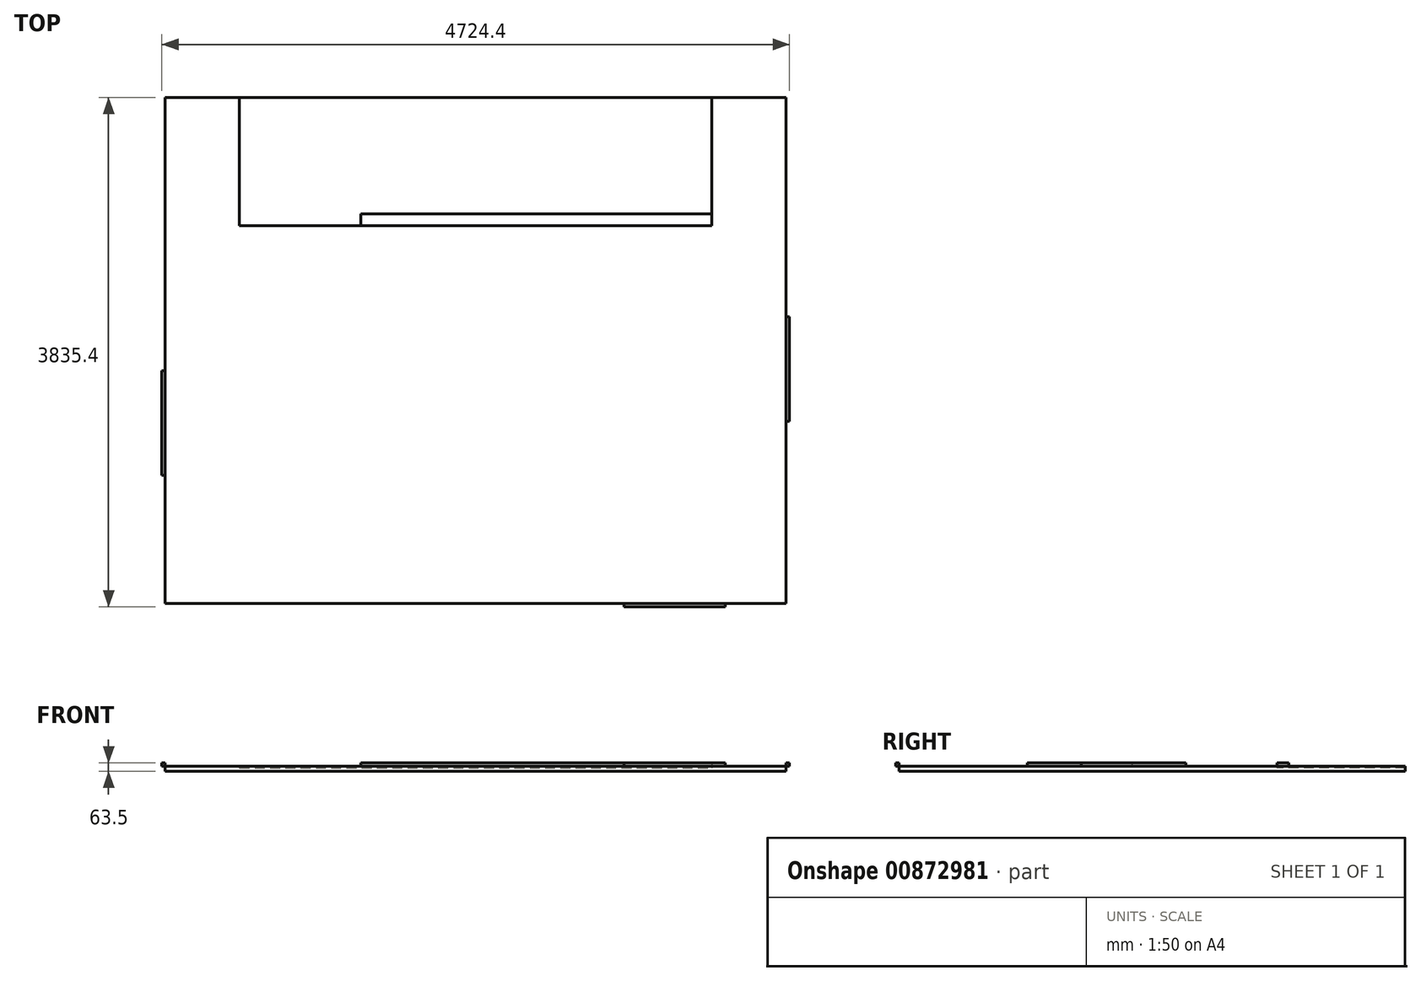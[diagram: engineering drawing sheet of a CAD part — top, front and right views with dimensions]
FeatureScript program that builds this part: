
annotation { "Feature Type Name" : "Feature", "Feature Type Description" : "" }
export const myFeature = defineFeature(function(context is Context, id is Id, definition is map)
    precondition{}
    {
        {
            var Q0;
            Q0=qCreatedBy(makeId("Top.planeOp"),FACE);
            var sketch = newSketch(context, id + "F0", { "sketchPlane" : qUnion([Q0])});
            skLineSegment(sketch, "E0", {"start": v(0, 0) * mm, "end": v(0, 3810) * mm});
            skLineSegment(sketch, "E1", {"start": v(0, 3810) * mm, "end": v(4673.6, 3810) * mm});
            skLineSegment(sketch, "E2", {"start": v(4673.6, 3810) * mm, "end": v(4673.6, 0) * mm});
            skLineSegment(sketch, "E3", {"start": v(4673.6, 0) * mm, "end": v(0, 0) * mm});
            skSolve(sketch);
        }
        {
            var Q0;
            Q0 = qSketchRegion(id + "F0", true);
            extrude(context, id + "F1", {"entities" : qUnion([Q0]), "depth" : 25.4 * mm, "offsetDistance" : 25.4 * mm});
        }
        {
            var Q0;
            Q0=makeQuery(id+"F1.opExtrude","CAP_FACE",FACE,{"disambiguationData":[OSD([sQuery(id+"F0.wireOp",EDGE,"E0"),sQuery(id+"F0.wireOp",EDGE,"E1"),sQuery(id+"F0.wireOp",EDGE,"E2"),sQuery(id+"F0.wireOp",EDGE,"E3")])],"isStart":false});
            var sketch = newSketch(context, id + "F2", { "sketchPlane" : qUnion([Q0])});
            skLineSegment(sketch, "E4", {"start": v(558.8, 3810) * mm, "end": v(558.8, 2844.8) * mm});
            skLineSegment(sketch, "E5", {"start": v(558.8, 2844.8) * mm, "end": v(4114.8, 2844.8) * mm});
            skLineSegment(sketch, "E6", {"start": v(4114.8, 2844.8) * mm, "end": v(4114.8, 3810) * mm});
            skLineSegment(sketch, "E7.0.0", {"start": v(0, 0) * mm, "end": v(4673.6, 0) * mm});
            skLineSegment(sketch, "E7.0.1", {"start": v(4673.6, 0) * mm, "end": v(4673.6, 3810) * mm});
            skLineSegment(sketch, "E7.0.2", {"start": v(4673.6, 3810) * mm, "end": v(0, 3810) * mm});
            skLineSegment(sketch, "E7.0.3", {"start": v(0, 3810) * mm, "end": v(0, 0) * mm});
            skSolve(sketch);
        }
        {
            var Q0;
            {var subQ1=sQuery(id+"F2.wireOp",EDGE,"E4");Q0=makeQuery(id+"F2.imprint","IMPRINT",FACE,{"disambiguationData":[TD([[makeQuery(id+"F2.imprint","IMPRINT",EDGE,{"derivedFrom":subQ1}),-1.0]])]});}
            extrude(context, id + "F3", {"entities" : qUnion([Q0]), "operationType" : NewBodyOperationType.ADD, "depth" : 12.7 * mm, "offsetDistance" : 25.4 * mm});
        }
        {
            var Q0;
            Q0=makeQuery(id+"F3.opExtrude","CAP_FACE",FACE,{"disambiguationData":[OSD([sQuery(id+"F2.wireOp",EDGE,"E4"),sQuery(id+"F2.wireOp",EDGE,"E5"),sQuery(id+"F2.wireOp",EDGE,"E6"),sQuery(id+"F2.wireOp",EDGE,"E7.0.0"),sQuery(id+"F2.wireOp",EDGE,"E7.0.1"),sQuery(id+"F2.wireOp",EDGE,"E7.0.2"),sQuery(id+"F2.wireOp",EDGE,"E7.0.3")])],"isStart":false});
            var sketch = newSketch(context, id + "F4", { "sketchPlane" : qUnion([Q0])});
            skLineSegment(sketch, "E8", {"start": v(4114.8, 2844.8) * mm, "end": v(1473.2, 2844.8) * mm});
            skLineSegment(sketch, "E9", {"start": v(1473.2, 2844.8) * mm, "end": v(1473.2, 2933.7) * mm});
            skLineSegment(sketch, "E10", {"start": v(1473.2, 2933.7) * mm, "end": v(4114.8, 2933.7) * mm});
            skLineSegment(sketch, "E11", {"start": v(4114.8, 2933.7) * mm, "end": v(4114.8, 2844.8) * mm});
            skLineSegment(sketch, "E12.0", {"start": v(4114.8, 2844.8) * mm, "end": v(4114.8, 3810) * mm});
            skLineSegment(sketch, "E13.0.0", {"start": v(558.8, 2844.8) * mm, "end": v(4114.8, 2844.8) * mm});
            skLineSegment(sketch, "E13.0.2", {"start": v(4114.8, 3810) * mm, "end": v(558.8, 3810) * mm});
            skLineSegment(sketch, "E13.0.3", {"start": v(558.8, 3810) * mm, "end": v(558.8, 2844.8) * mm});
            skLineSegment(sketch, "E14.0", {"start": v(4673.6, 3810) * mm, "end": v(4673.6, 0) * mm});
            skSolve(sketch);
        }
        {
            var Q0;
            {var subQ0=sQuery(id+"F4.wireOp",EDGE,"E9");Q0=makeQuery(id+"F4.imprint","IMPRINT",FACE,{"disambiguationData":[TD([[makeQuery(id+"F4.imprint","IMPRINT",EDGE,{"derivedFrom":subQ0}),-1.0]])]});}
            extrude(context, id + "F5", {"entities" : qUnion([Q0]), "depth" : 25.4 * mm, "offsetDistance" : 25.4 * mm});
        }
        {
            var Q0;
            Q0=makeQuery(id+"F3.opExtrude","CAP_FACE",FACE,{"disambiguationData":[OSD([sQuery(id+"F2.wireOp",EDGE,"E4"),sQuery(id+"F2.wireOp",EDGE,"E5"),sQuery(id+"F2.wireOp",EDGE,"E6"),sQuery(id+"F2.wireOp",EDGE,"E7.0.0"),sQuery(id+"F2.wireOp",EDGE,"E7.0.1"),sQuery(id+"F2.wireOp",EDGE,"E7.0.2"),sQuery(id+"F2.wireOp",EDGE,"E7.0.3")])],"isStart":false});
            var sketch = newSketch(context, id + "F6", { "sketchPlane" : qUnion([Q0])});
            skLineSegment(sketch, "E15.bottom", {"start": v(0, 965.2) * mm, "end": v(-25.4, 965.2) * mm});
            skLineSegment(sketch, "E15.top", {"start": v(0, 1752.6) * mm, "end": v(-25.4, 1752.6) * mm});
            skLineSegment(sketch, "E15.left", {"start": v(0, 965.2) * mm, "end": v(0, 1752.6) * mm});
            skLineSegment(sketch, "E15.right", {"start": v(-25.4, 965.2) * mm, "end": v(-25.4, 1752.6) * mm});
            skLineSegment(sketch, "E16.0.0", {"start": v(4114.8, 3810) * mm, "end": v(4114.8, 2844.8) * mm});
            skLineSegment(sketch, "E16.0.1", {"start": v(4114.8, 2844.8) * mm, "end": v(558.8, 2844.8) * mm});
            skLineSegment(sketch, "E16.0.2", {"start": v(558.8, 2844.8) * mm, "end": v(558.8, 3810) * mm});
            skLineSegment(sketch, "E16.0.3", {"start": v(558.8, 3810) * mm, "end": v(0, 3810) * mm});
            skLineSegment(sketch, "E16.0.4", {"start": v(0, 3810) * mm, "end": v(0, 0) * mm});
            skLineSegment(sketch, "E16.0.5", {"start": v(0, 0) * mm, "end": v(4673.6, 0) * mm});
            skLineSegment(sketch, "E16.0.6", {"start": v(4673.6, 0) * mm, "end": v(4673.6, 3810) * mm});
            skLineSegment(sketch, "E16.0.7", {"start": v(4673.6, 3810) * mm, "end": v(4114.8, 3810) * mm});
            skSolve(sketch);
        }
        {
            var Q0;
            {var subQ0=sQuery(id+"F6.wireOp",EDGE,"E15.bottom");Q0=makeQuery(id+"F6.imprint","IMPRINT",FACE,{"disambiguationData":[TD([[makeQuery(id+"F6.imprint","IMPRINT",EDGE,{"derivedFrom":subQ0}),-1.0]])]});}
            extrude(context, id + "F7", {"entities" : qUnion([Q0]), "depth" : 25.4 * mm, "offsetDistance" : 25.4 * mm});
        }
        {
            var Q0;
            Q0=makeQuery(id+"F3.opExtrude","CAP_FACE",FACE,{"disambiguationData":[OSD([sQuery(id+"F2.wireOp",EDGE,"E4"),sQuery(id+"F2.wireOp",EDGE,"E5"),sQuery(id+"F2.wireOp",EDGE,"E6"),sQuery(id+"F2.wireOp",EDGE,"E7.0.0"),sQuery(id+"F2.wireOp",EDGE,"E7.0.1"),sQuery(id+"F2.wireOp",EDGE,"E7.0.2"),sQuery(id+"F2.wireOp",EDGE,"E7.0.3")])],"isStart":false});
            var sketch = newSketch(context, id + "F8", { "sketchPlane" : qUnion([Q0])});
            skLineSegment(sketch, "E17.0", {"start": v(4673.6, 3810) * mm, "end": v(4673.6, 0) * mm});
            skLineSegment(sketch, "E18.bottom", {"start": v(4673.6, 2159) * mm, "end": v(4699, 2159) * mm});
            skLineSegment(sketch, "E18.top", {"start": v(4673.6, 1371.6) * mm, "end": v(4699, 1371.6) * mm});
            skLineSegment(sketch, "E18.left", {"start": v(4673.6, 2159) * mm, "end": v(4673.6, 1371.6) * mm});
            skLineSegment(sketch, "E18.right", {"start": v(4699, 2159) * mm, "end": v(4699, 1371.6) * mm});
            skLineSegment(sketch, "E19.0", {"start": v(4673.6, 0) * mm, "end": v(0, 0) * mm});
            skLineSegment(sketch, "E20.bottom", {"start": v(4216.4, 0) * mm, "end": v(3454.4, 0) * mm});
            skLineSegment(sketch, "E20.top", {"start": v(4216.4, -25.4) * mm, "end": v(3454.4, -25.4) * mm});
            skLineSegment(sketch, "E20.left", {"start": v(4216.4, 0) * mm, "end": v(4216.4, -25.4) * mm});
            skLineSegment(sketch, "E20.right", {"start": v(3454.4, 0) * mm, "end": v(3454.4, -25.4) * mm});
            skSolve(sketch);
        }
        {
            var Q0;
            Q0 = qSketchRegion(id + "F8", true);
            extrude(context, id + "F9", {"entities" : qUnion([Q0]), "depth" : 25.4 * mm, "offsetDistance" : 25.4 * mm});
        }
    });
